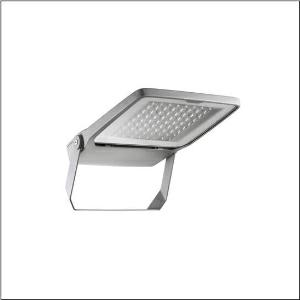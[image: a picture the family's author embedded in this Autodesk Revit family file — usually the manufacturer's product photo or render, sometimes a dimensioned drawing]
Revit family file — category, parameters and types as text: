
# Revit family: floodlight_fl_20_mini___pl61_5xa7671c2c1ac_aaab
name_source: partatom
category: Lighting Fixtures
units: mm (PartAtom-declared; Revit-internal decimal feet)

## family parameters
Cut with Voids When Loaded = No
Host = Face
Light Source = No
Part Type = Normal
Room Calculation Point = No
Round Connector Dimension = Use Diameter
Shared = No

## types (1)
- Floodlight FL 20 mini  PL61 (1 x LED 4000K / CRI = 70 (unbekannt), 12430 lm, 4000K)
    Apparent Load = 96 VA
    CIE Flux Codes = 33 65 98 100 100
    Color Rendering = 70
    Color Temperature = 4000K
    Default Elevation = 1800 mm
    Description = Floodlight FL 20 mini, floodlight, primary light control with lens, of plastic, primary optical cover: protective disc, of toughened safety glass, transparent, light distribution: PL61, light emission: direct distribution, primary light characteristic: asymmetric, installation type: surface-mounted, LED, High Power LED, rated luminous flux: 12.430lm, luminous efficacy: 130lm/W, light colour: 740, colour temperature: 4000K, control gear: ECG Basic, control: power reduction, overheat protection, electronic power reduction, with terminal, 5-pole, max. 2.5mm², mains connection: 220..240V, AC, 50/60Hz, rated input power: 96W, LED unit, of diecast aluminium, powder-coated, Siteco® metallic grey (DB 702S), corrosivity category C5 mid according to DIN EN ISO 12944, incl. 1x M20 cable gland for cable Ø 6.5..12mm, length: 446mm, width: 355mm, height: 62mm, housing frame, of diecast aluminium, powder-coated, Siteco® metallic grey (DB 702S), mounting bracket, of steel, powder-coated, Siteco® metallic grey (DB 702S), ON/OFF, protection rating (complete): IP66, insulation class (complete): insulation class I (protective earthing), certification: CE, ENEC, VDE, protection symbol: D, permissible operating ambient temperature: -40..+40°C, permissible operating ambient temperature for outdoor applications: -40..+50°C, standard: DIN EN 12944, packaging unit: 1 piece

Light Distribution: PL61
    Height = 62 mm  [stored 0.203412 ft]
    Lamp = 1 x LED 4000K / CRI >= 70 (unbekannt)
    Lamp Light Flux = 12430 lm
    Lamp count = 1
    Length = 467 mm
    Luminous efficacy = 130 lm/W
    Manufacturer = Siteco
    ModVariant = No
    Model = 5XA7671C2C1AC
    Mounting Place = Wall
    Mounting Type = Surface mounted
    Number of Poles = 1
    OnlyDefault = Yes
    Power Factor = 1
    Product Name = Floodlight FL 20 mini | PL61
    Product group = floodlight | wall mounted
    ProductGroupID = 2001
    Protection Class = Protection class I
    Protection Degree = IP 66
    RLX_Detail_Level = 1
    RLX_Emergency_Light_Flux = 0 lm
    RLX_Emergency_Type = 0
    RLX_Emergency_Type_DB = No
    RlxData = <blob elided: 71005 chars, md5=b02974ef>
    Socket = socket
    Standby Power = 0 W
    System Light Flux = 12430 lm
    System Power = 96 W
    Type Comments = Product without accessories
    Type Image = l_1005948.jpg
    URL = http://relux.com
    VarID = ---
    Voltage = 0 V
    Weight = 0.00 kg
    Width = 335 mm

note: [stored X ft] marks values corroborated as IEEE doubles in the binary element streams (Revit-internal decimal feet)

## geometry (parser evidence)
native form markers: Blend x4, Sweep x12
no freeform markers — native parametric forms only
